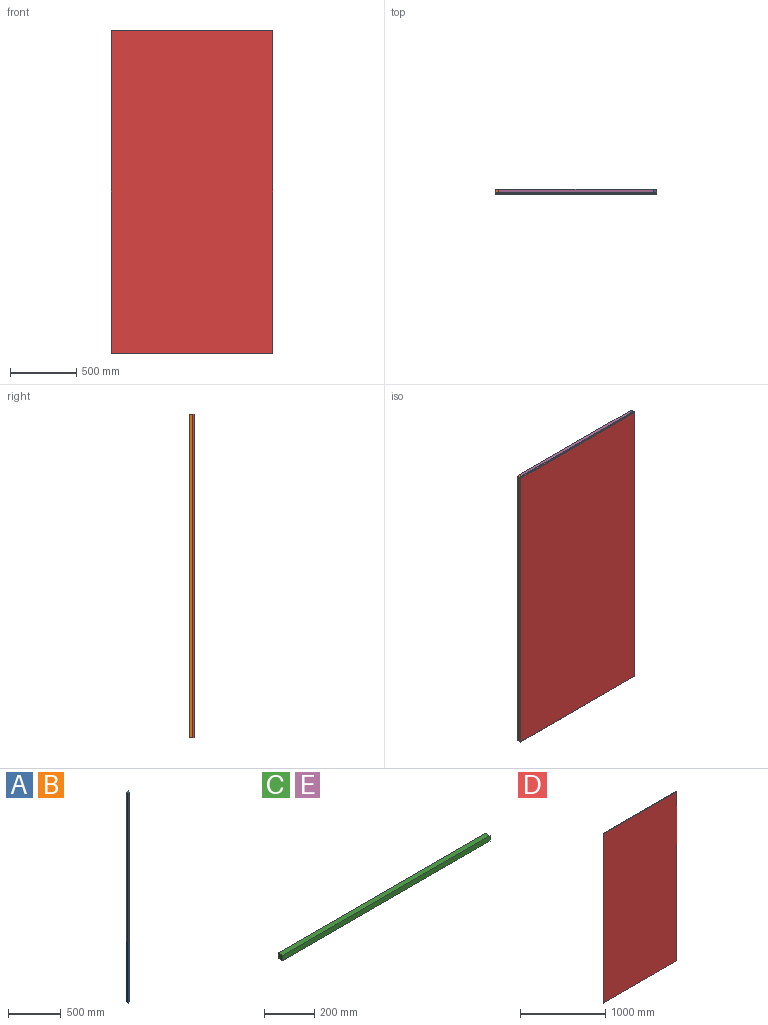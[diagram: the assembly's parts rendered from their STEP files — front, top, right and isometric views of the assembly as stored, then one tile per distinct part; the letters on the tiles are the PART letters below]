
ASSEMBLY  parts=5 mates=4
PART A: 6 faces, bbox 25.4x25.4x2438.4 mm
  f0: plane 25.4x25.4mm, normal (0,0,-1), area 645.2mm2, adj f1,f2,f3,f4
  f1: plane 2438.4x25.4mm, normal (0,-1,0), area 61935.4mm2, adj f0,f2,f4,f5
  f2: plane 2438.4x25.4mm, normal (1,0,0), area 61935.4mm2, adj f0,f1,f3,f5
  f3: plane 2438.4x25.4mm, normal (0,1,0), area 61935.4mm2, adj f0,f2,f4,f5
  f4: plane 2438.4x25.4mm, normal (-1,0,0), area 61935.4mm2, adj f0,f1,f3,f5
  f5: plane 25.4x25.4mm, normal (0,0,1), area 645.2mm2, adj f1,f2,f3,f4
PART B: same geometry as A
PART C: 6 faces, bbox 1168.4x25.4x25.4 mm
  f0: plane 1168.4x25.4mm, normal (0,0,-1), area 29677.4mm2, adj f1,f3,f4,f5
  f1: plane 1168.4x25.4mm, normal (0,-1,0), area 29677.4mm2, adj f0,f2,f4,f5
  f2: plane 1168.4x25.4mm, normal (0,0,1), area 29677.4mm2, adj f1,f3,f4,f5
  f3: plane 1168.4x25.4mm, normal (0,1,0), area 29677.4mm2, adj f0,f2,f4,f5
  f4: plane 25.4x25.4mm, normal (-1,0,0), area 645.2mm2, adj f0,f1,f2,f3
  f5: plane 25.4x25.4mm, normal (1,0,0), area 645.2mm2, adj f0,f1,f2,f3
PART D: 10 faces, bbox 1219.2x12.7x2438.4 mm
  f0: plane 2438.4x10.16mm, normal (1,0,0), area 24774.1mm2, adj f1,f3,f5,f6
  f1: plane 1219.2x10.16mm, normal (0,0,1), area 12387.1mm2, adj f0,f2,f5,f7
  f2: plane 2438.4x10.16mm, normal (-1,0,0), area 24774.1mm2, adj f1,f3,f5,f9
  f3: plane 1219.2x10.16mm, normal (0,0,-1), area 12387.1mm2, adj f0,f2,f5,f8
  f4: plane 2433.32x1214.12mm, normal (0,-1,0), area 2954342.5mm2, adj f6,f7,f8,f9
  f5: plane 2438.4x1219.2mm, normal (0,1,0), area 2972897.3mm2, adj f0,f1,f2,f3
  f6: cylinder r=2.54mm len=2438.4mm, axis (0,0,-1), area 9721.4mm2, adj f0,f4,f7,f8
  f7: cylinder r=2.54mm len=1219.2mm, axis (1,0,0), area 4857mm2, adj f1,f4,f6,f9
  f8: cylinder r=2.54mm len=1219.2mm, axis (-1,0,0), area 4857mm2, adj f3,f4,f6,f9
  f9: cylinder r=2.54mm len=2438.4mm, axis (0,0,1), area 9721.4mm2, adj f2,f4,f7,f8
PART E: same geometry as C
PLACE A t=(609.6,0,1219.2)mm
PLACE B t=(-584.2,0,1219.2)mm
PLACE C t=(609.6,0,-1193.8)mm
PLACE D t=(609.6,0,1219.2)mm
PLACE E t=(609.6,0,1219.2)mm
MATE fastened C.f4 <-> B.f2  axis (-1,0,0) through (25.4,0,0)mm
MATE fastened A.f1 <-> D.f5  axis (0,-1,0) through (1219.2,0,2438.4)mm
MATE fastened E.f5 <-> A.f4  axis (1,0,0) through (1193.8,25.4,2438.4)mm
MATE fastened B.f2 <-> E.f4  axis (1,0,0) through (25.4,0,2438.4)mm
